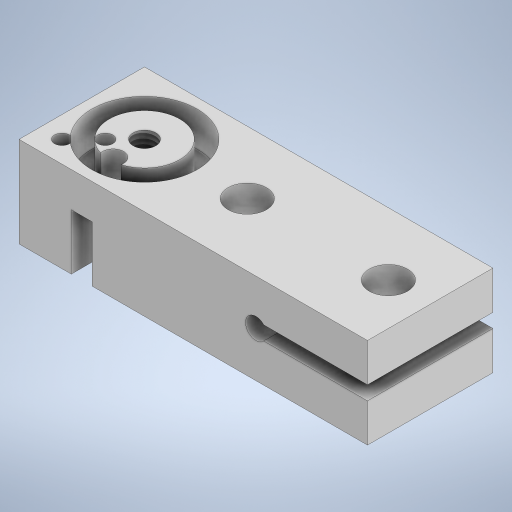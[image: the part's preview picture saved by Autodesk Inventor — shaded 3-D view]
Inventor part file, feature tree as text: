
AUTODESK INVENTOR PART (.ipt)
format: ipt  version: 2024 (Build 280153000, 153)  size: 306,688 bytes
history: native  units: in
note: dims shown in document units (in); Inventor stores cm internally (conversion verified against a paired STEP export)
features: extrude x3, sketch x3, hole x3
ambient origin geometry x8: Origin, YZ Plane, XZ Plane, XY Plane, X Axis, Y Axis, Z Axis, Center Point
bodies: Solid1 (feature_tree)
feature tree (9):
  extrude  "Extrusion1"  Depth=0.5118in
  sketch  "Sketch2"  dims[d2=0.6299in d3=0.1181in]
  hole  "Hole1"  [1 undecoded]
  extrude  "Extrusion2"  Depth=0.0394in
  sketch  "Sketch3"  dims[d4=0.0394in d5=0.0394in d6=0.7087in d7=0.0in d8=0.2362in d9=0.7972in d10=0.3445in d11=0.3445in d12=0.2953in d13=0.0591in d14=0.1969in d15=0.1181in d16=0.2165in d17=0.1575in d18=0.3937in d19=0.2244in d20=90.0deg d21=0.315in d22=0.8108in d23=0.315in d24=0.0in d25=45.0deg d26=0.5945in d27=0.3976in d28=0.1575in d29=0.0984in d30=0.1181in d31=0.0421in d32=0.0854in d33=0.1718in d34=0.0854in d35=0.1969in d36=0.0in d37=0.1276in d38=0.315in d39=0.1575in d40=0.0787in d41=90.0deg d42=0.3346in d43=0.8108in d44=0.0854in d45=0.315in d46=0.1575in d47=0.0787in d48=90.0deg d49=0.3346in d50=0.0in]
  extrude  "Extrusion3"  Depth=0.7087in TaperAngle=0.0deg
  hole  "Hole2"  [1 undecoded]
  hole  "Hole3"  [1 undecoded]
  sketch  "Sketch1"  dims[d0=1.9685in d1=0.5118in]
note: 3 required parameter values undecoded (feature->parameter linkage not recoverable at this tier; creation-order binding heuristic only, values carry confidence <= 0.55)
